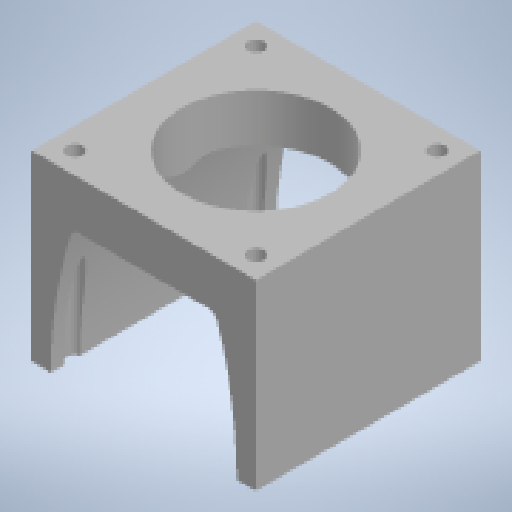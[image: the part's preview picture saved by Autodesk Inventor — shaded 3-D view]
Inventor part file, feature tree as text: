
AUTODESK INVENTOR PART (.ipt)
format: ipt  version: 2023 (Build 270158000, 158)  size: 479,232 bytes
history: native  units: mm
features: sketch x15, extrude x14, reference x7, other x5, mirror x4, projected_geometry x3, plane x2, pattern_linear x1, chamfer x1, fillet x1
ambient origin geometry x8: Origin, YZ Plane, XZ Plane, XY Plane, X Axis, Y Axis, Z Axis, Center Point
bodies: Solid1 (feature_tree)
feature tree (53):
  extrude  "Extrusion1"  Depth=58.4mm
  extrude  "Extrusion2"  Depth=4.2mm
  extrude  "Extrusion3"  Depth=2.0mm
  extrude  "Extrusion4"  Depth=5.0mm
  extrude  "Extrusion5"  Depth=7.5mm TaperAngle=0.0deg
  extrude  "Extrusion6"  Depth=10.0mm
  extrude  "Extrusion7"  Depth=2.0mm
  plane  "Work Plane1"
  mirror  "Mirror1"
  extrude  "Extrusion8"  Depth=1.0mm
  extrude  "Extrusion9"  Depth=0.15mm
  sketch  "Sketch9"  dims[d23=1.0mm d24=0.15mm]
  extrude  "Extrusion10"  Depth=5.0mm
  extrude  "Extrusion11"  Depth=10.1mm TaperAngle=0.0deg
  plane  "Work Plane2"
  extrude  "Extrusion12"  Depth=2.5mm
  mirror  "Mirror2"
  extrude  "Extrusion13"  Depth=4.1mm TaperAngle=0.0deg
  pattern_linear  "Rectangular Pattern1"  Spacing1=0.25mm  [1 undecoded]
  mirror  "Mirror3"
  extrude  "Extrusion14"  Depth=2.0mm TaperAngle=0.0deg
  mirror  "Mirror4"
  chamfer  "Chamfer1"  Distance=8.5mm
  fillet  "Fillet1"  Radius=5.0mm
  sketch  "Sketch1"  dims[d2=58.4mm d3=38.6mm]
  sketch  "Sketch2"  dims[d4=47.14mm d5=4.2mm]
  sketch  "Sketch3"  dims[d6=7.5mm d7=0.0mm d9=2.0mm]
  projected_geometry  "Projected Loop1"
  reference  "Reference1"
  sketch  "Sketch4"  dims[d10=5.0mm d12=5.0mm]
  reference  "Reference2"
  reference  "Reference3"
  sketch  "Sketch5"  dims[d13=38.0mm d14=7.5mm d15=0.0mm]
  sketch  "Sketch6"  dims[d16=10.0mm d17=0.0mm d18=0.5mm]
  reference  "Reference4"
  sketch  "Sketch7"  dims[d19=5.0mm d20=2.0mm]
  sketch  "Sketch8"  dims[d21=1.0mm d22=1.0mm]
  reference  "Reference5"
  reference  "Reference6"
  reference  "Reference7"
  sketch  "Sketch10"  dims[d25=5.0mm d26=5.0mm]
  sketch  "Sketch11"  dims[d27=4.35mm d28=0.0mm d29=10.1mm d30=0.0mm]
  projected_geometry  "Projected Loop2"
  sketch  "Sketch12"  dims[d31=0.15mm d32=2.5mm]
  sketch  "Sketch13"  dims[d33=10.1mm d34=0.0mm d35=4.1mm d36=0.0mm]
  sketch  "Sketch14"  dims[d37=0.25mm]
  projected_geometry  "Projected Loop3"
  sketch  "Sketch15"  dims[d38=0.25mm d39=0.25mm d40=30.0mm d41=0.0mm d42=8.5mm d43=5.0mm d44=14.75mm d45=0.0mm d46=217.5mm d47=0.0mm d48=5.7625mm d50=5.5mm d51=15.0mm d52=217.5mm d53=0.0mm d54=-5.0mm d55=11.0mm d56=217.5mm d57=0.0mm d58=3.0mm d59=0.0mm d60=50.0mm d62=10.0mm d63=10.0mm d64=0.0mm d65=2.0mm d66=2.0mm d67=45.0deg d68=2.0mm]
  other  "<userpath>\Desktop\CNC_Project\FrameV4.iam"
  other  "FrameV4.iam"
  other  "Z_Gantry_Plate_Spaced:1"
  other  "Z_Gantry_Plate:1"
  other  "BK10:2"
note: 1 required parameter value undecoded (feature->parameter linkage not recoverable at this tier; creation-order binding heuristic only, values carry confidence <= 0.55)
